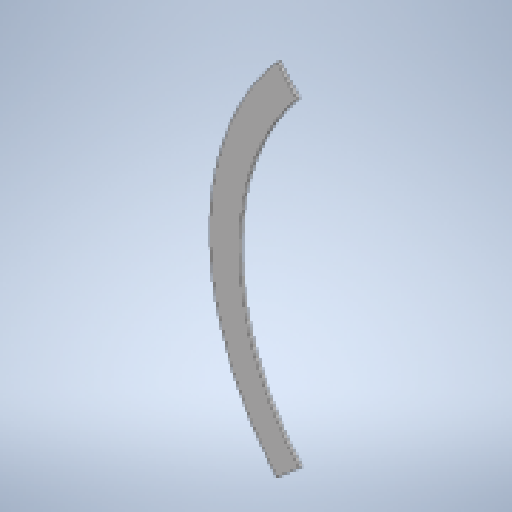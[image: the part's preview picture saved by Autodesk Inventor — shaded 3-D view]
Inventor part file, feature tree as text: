
AUTODESK INVENTOR PART (.ipt)
format: ipt  version: 2023 (Build 270158000, 158)  size: 138,240 bytes
history: native  units: in
note: dims shown in document units (in); Inventor stores cm internally (conversion verified against a paired STEP export)
features: other x1, extrude x1, sketch x1
ambient origin geometry x8: Origin, YZ Plane, XZ Plane, XY Plane, X Axis, Y Axis, Z Axis, Center Point
bodies: Body1 (feature_tree)
feature tree (3):
  other  "Bryła1"
  extrude  "Wyciągnięcie proste1"  Depth=0.0079in TaperAngle=0.0deg
  sketch  "Szkic1"
